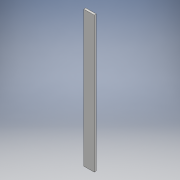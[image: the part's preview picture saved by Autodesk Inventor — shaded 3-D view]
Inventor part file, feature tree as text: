
AUTODESK INVENTOR PART (.ipt)
format: ipt  version: 2017 (Build 210142000, 142)  size: 92,160 bytes
history: native  units: mm
features: other x1, extrude x1, sketch x1
ambient origin geometry x8: Origin, YZ Plane, XZ Plane, XY Plane, X Axis, Y Axis, Z Axis, Center Point
bodies: Body1 (feature_tree)
feature tree (3):
  other  "Твердое тело1"
  extrude  "Выдавливание1"  Depth=20.0mm
  sketch  "Эскиз1"
